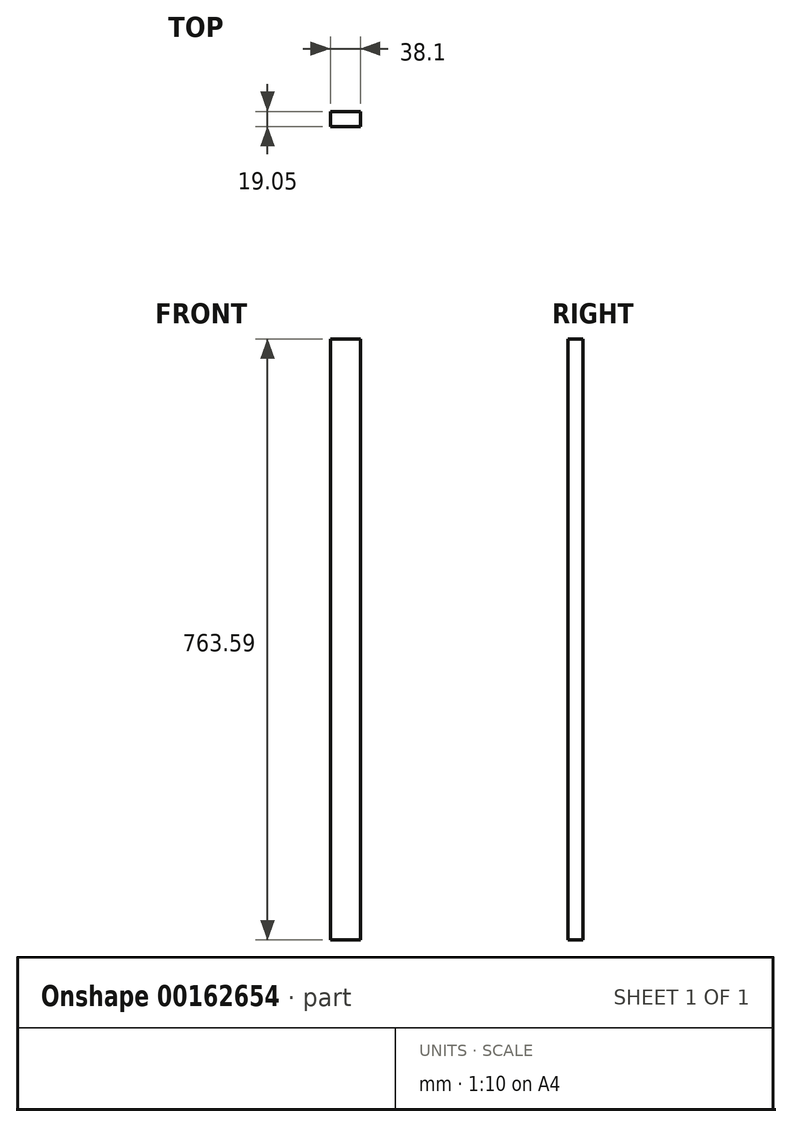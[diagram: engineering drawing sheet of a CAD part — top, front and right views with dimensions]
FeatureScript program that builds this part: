
annotation { "Feature Type Name" : "Feature", "Feature Type Description" : "" }
export const myFeature = defineFeature(function(context is Context, id is Id, definition is map)
    precondition{}
    {
        {
            var Q0;
            Q0=qCreatedBy(makeId("Front.planeOp"),FACE);
            var sketch = newSketch(context, id + "F0", { "sketchPlane" : qUnion([Q0])});
            skLineSegment(sketch, "E0.bottom", {"start": v(23.46, 516.04) * mm, "end": v(61.56, 516.04) * mm});
            skLineSegment(sketch, "E0.top", {"start": v(23.46, -247.55) * mm, "end": v(61.56, -247.55) * mm});
            skLineSegment(sketch, "E0.left", {"start": v(23.46, 516.04) * mm, "end": v(23.46, -247.55) * mm});
            skLineSegment(sketch, "E0.right", {"start": v(61.56, 516.04) * mm, "end": v(61.56, -247.55) * mm});
            skSolve(sketch);
        }
        {
            var Q0;
            Q0 = qSketchRegion(id + "F0", true);
            extrude(context, id + "F1", {"entities" : qUnion([Q0]), "depth" : 19.05 * mm});
        }
    });
